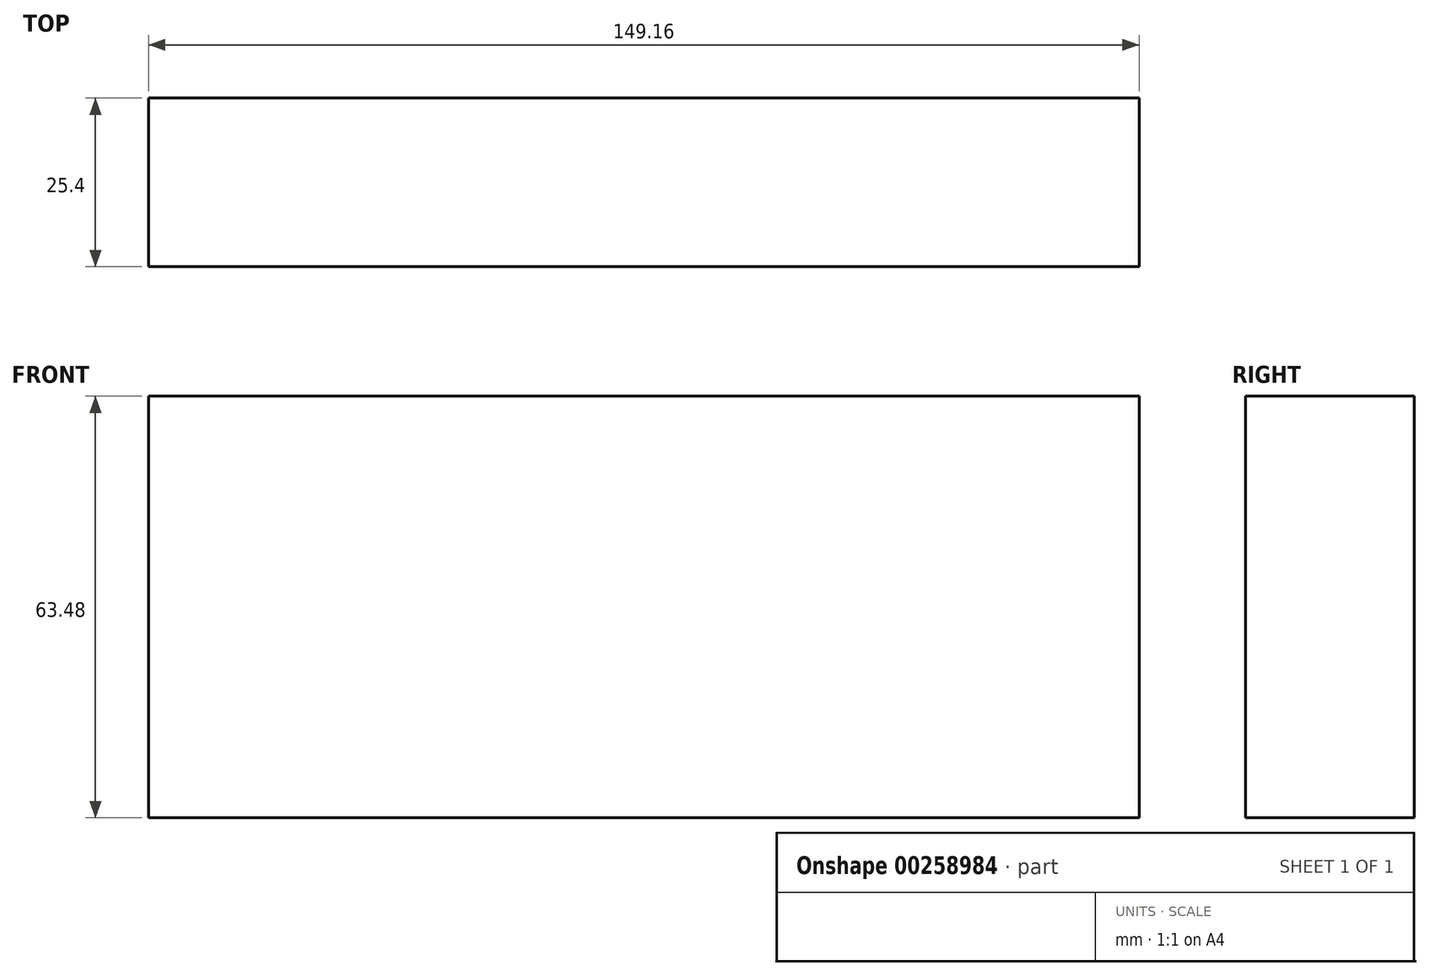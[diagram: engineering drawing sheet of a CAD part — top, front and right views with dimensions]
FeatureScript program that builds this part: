
annotation { "Feature Type Name" : "Feature", "Feature Type Description" : "" }
export const myFeature = defineFeature(function(context is Context, id is Id, definition is map)
    precondition{}
    {
        {
            var Q0;
            Q0=qCreatedBy(makeId("Front.planeOp"),FACE);
            var sketch = newSketch(context, id + "F0", { "sketchPlane" : qUnion([Q0])});
            skLineSegment(sketch, "E0", {"start": v(48.54, 41.08) * mm, "end": v(48.54, -16.39) * mm});
            skLineSegment(sketch, "E1", {"start": v(48.54, -16.39) * mm, "end": v(-100.62, -16.39) * mm});
            skLineSegment(sketch, "E2", {"start": v(-100.62, -16.39) * mm, "end": v(-100.62, 47.1) * mm});
            skLineSegment(sketch, "E3", {"start": v(-100.62, 47.1) * mm, "end": v(48.54, 47.1) * mm});
            skLineSegment(sketch, "E4", {"start": v(48.54, 47.1) * mm, "end": v(48.54, 41.08) * mm});
            skSolve(sketch);
        }
        {
            var Q0;
            Q0=makeQuery(id+"F0.imprint","IMPRINT",FACE,{"disambiguationData":[TD([[makeQuery(id+"F0.imprint","IMPRINT",EDGE,{"derivedFrom":sQuery(id+"F0.wireOp",EDGE,"E0")}),-1.0]])]});
            extrude(context, id + "F1", {"entities" : qUnion([Q0]), "depth" : 25.4 * mm});
        }
    });
